# Revit family: QF_ELECTROLUXPROFESSIONAL_1L059Y_TD6-14_G
name_source: partatom
category: Attrezzature speciali
units: mm (PartAtom-declared; Revit-internal decimal feet)

## family parameters
Basato su piano di lavoro = No
Condiviso = No
Punto di calcolo locali = No
Quota connettore circolare = Usa diametro
Sempre verticale = Sì
Taglio con vuoti quando caricato = No
Tipo di parte = Normale

## types (36) — shared parameters
Depth Actual = 965 mm  [stored 3.16601 ft]
Height Actual = 1771 mm  [stored 5.81037 ft]
Latent Heat Output = 0.0
Length Actual = 790 mm  [stored 2.59186 ft]
Modello = TD6-14
Produttore = Electrolux Professional
Sensible Heat Output = 0.0
URL = www.electroluxprofessional.com
Weight = 222
zero-valued in all types: Prospetto di default, Steam Pounds per Hour

## per-type parameters (varying)
| type | Cycle | Descrizione | Gas KW | Item Number | Phase | Volts | Watts |
| 9873730032 | 50 Hz | TUMBLE DRYER TD6-14 14KG SST DRUM GAS 13,5KW 400/50/3 COMPASS PRO 6G82 EU SILVER DO.RIGHT STOP DISCON. | 13.5 | 1L0EDB | 3 | 400 V | 1000 W |
| 9873730150 | 50 Hz | TUMBLE DRYER TD6-14 14KG SST DRUM GAS 13,5KW 400/50/3N COMPASS PRO 6G81 EU SILVER DO.RIGHT MB STOP DISCON. | 13.5 | 1LSPA5 | 3 | 400 V | 1000 W |
| 9873730198 | 60 Hz | TUMBLE DRYER TD6-14 14KG GALVA.DRUM GAS 13,5KW 220/60/1N COMPASS PRO 6L80 EU SILVER DO.LEFT | 0 | 1L0H79 | 1 | 220 V | 1200 W |
| 9873730120 | 60 Hz | TUMBLE DRYER TD6-14 14KG GALVA.DRUM GAS 13,5KW 240/60/1N COMPASS PRO 6G82 EU SILVER DO.RIGHT STOP DISCON. | 13.5 | 1LSNV5 | 1 | 240 V | 1200 W |
| 9873730158 | 50 Hz | TUMBLE DRYER TD6-14 14KG GALVA.DRUM GAS 13,5KW 400/50/3N COMPASS PRO 6L80 EU SILVER DO.RIGHT.INS. EXT.PM. 2.I/O | 0 | 1L82DG | 3 | 400 V | 1000 W |
| 9873730108 | 50 Hz | TUMBLE DRYER TD6-14 14KG GALVA.DRUM GAS 13,5KW 400/50/3 COMPASS PRO 6G82 EU SILVER DO.RIGHT STOP DISCON. | 13.5 | 1LSNPR | 3 | 400 V | 1000 W |
| 9873730069 | 50 Hz | TUMBLE DRYER TD6-14 14KG SST DRUM GAS 13,5KW 400/50/3 COMPASS PRO 6L80 EU SILVER DO.RIGHT EXT.PM. DISCON. 2.I/O | 13.5 | 1LSN41 | 3 | 400 V | 1000 W |
| 9873730155 | 50 Hz | TUMBLE DRYER TD6-14 14KG SST DRUM GAS 13,5KW 400/50/3N COMPASS PRO 6L80 EU SILVER DO.RIGHT EXT.PM. DISCON. 2.I/O | 13.5 | 1LSPAA | 3 | 400 V | 1000 W |
| 9873730175 | 60 Hz | TUMBLE DRYER TD6-14 14KG GALVA.DRUM GAS 13,5KW 220/60/3 COMPASS PRO 6G81 EU SILVER DO.LEFT.INS. MB STOP DISCON. | 13.5 | 1L826B | 3 | 220 V | 1000 W |
| 9873730115 | 50 Hz | TUMBLE DRYER TD6-14 14KG GALVA.DRUM GAS 13,5KW 400/50/3 COMPASS PRO 6L80 EU SILVER DO.RIGHT | 13.5 | 1LSNSB | 3 | 400 V | 1000 W |
| 9873730152 | 50 Hz | TUMBLE DRYER TD6-14 14KG GALVA.DRUM GAS 13,5KW 400/50/3N COMPASS PRO 6G81 EU SILVER DO.RIGHT.INS. MB STOP DISCON. | 13.5 | 1LSPA7 | 3 | 400 V | 1000 W |
| 9873730014 | 50 Hz | TUMBLE DRYER TD6-14 14KG GALVA.DRUM GAS 13,5KW 400/50/3 COMPASS PRO 6G81 EU SILVER DO.RIGHT.INS. MB STOP DISCON. | 13.5 | 1L0E92 | 3 | 400 V | 1000 W |
| 9873730024 | 50 Hz | TUMBLE DRYER TD6-14 14KG GALVA.DRUM GAS 13,5KW 400/50/3 COMPASS PRO 6G81 EU SILVER DO.RIGHT MB STOP DISCON. | 13.5 | 1LSN2L | 3 | 400 V | 1000 W |
| 9873730083 | 50 Hz | TUMBLE DRYER TD6-14 14KG GALVA.DRUM GAS 13,5KW 400/50/3N COMPASS PRO 6G81 EU SILVER DO.RIGHT MB STOP DISCON. | 13.5 | 1LSN57 | 3 | 400 V | 1000 W |
| 9873730013 | 50 Hz | TUMBLE DRYER TD6-14 14KG GALVA.DRUM GAS 13,5KW 400/50/3 COMPASS PRO 6L80 EU SILVER DO.RIGHT.INS. EXT.PM. 2.I/O | 13.5 | 1L0E91 | 3 | 400 V | 1000 W |
| 9873730200 | 50 Hz | TUMBLE DRYER TD6-14 14KG SST DRUM GPL 13,5KW 200/50/3 COMPASS PRO 6G86 JP SILVER DO.RIGHT DISCON. | 0 | 1L0H7S | 3 | 200 V | 1000 W |
| 9873730033 | 50 Hz | TUMBLE DRYER TD6-14 14KG SST DRUM GAS 13,5KW 400/50/3 COMPASS PRO 6G81 EU SILVER DO.RIGHT MB STOP DISCON. | 13.5 | 1L0EDC | 3 | 400 V | 1000 W |
| 9873730197 | 60 Hz | TUMBLE DRYER TD6-14 14KG SST DRUM GPL 13,5KW 200/60/3 COMPASS PRO 6G86 JP SILVER DO.RIGHT DISCON. | 0 | 1LT5ZE | 3 | 200 V | 1000 W |
| 9873730107 | 50 Hz | TUMBLE DRYER TD6-14 14KG GALVA.DRUM GAS 13,5KW 230/50/1N COMPASS PRO 6G82 EU SILVER DO.RIGHT STOP DISCON. | 13.5 | 1LSNJN | 1 | 230 V | 1200 W |
| 9873730086 | 50 Hz | TUMBLE DRYER TD6-14 14KG GALVA.DRUM GAS 13,5KW 400/50/3 COMPASS PRO 6L80 EU SILVER DO.RIGHT EXT.PM. DISCON. 2.I/O | 13.5 | 1L8216 | 3 | 400 V | 1000 W |
| 9873730036 | 50 Hz | TUMBLE DRYER TD6-14 14KG GALVA.DRUM GAS 13,5KW 415/50/3N COMPASS PRO 6G82 EU SILVER DO.LEFT STOP DISCON. | 13.5 | 1L0EDR | 3 | 415 V | 1000 W |
| 9873730085 | 50 Hz | TUMBLE DRYER TD6-14 14KG GALVA.DRUM GAS 13,5KW 400/50/3N COMPASS PRO 6G81 EU SILVER DO.RIGHT.INS. ELS-NETW. MB STOP DISC | 13.5 | 1LSN61 | 3 | 400 V | 1000 W |
| 9873730151 | 50 Hz | TUMBLE DRYER TD6-14 14KG SST DRUM GAS 13,5KW 400/50/3N COMPASS PRO 6G82 EU SILVER DO.RIGHT STOP DISCON. | 13.5 | 1LSPA6 | 3 | 400 V | 1000 W |
| 9873730055 | 50 Hz | TUMBLE DRYER TD6-14 14KG GALVA.DRUM GAS 13,5KW 230/50/1N COMPASS PRO 6G81 EU SILVER DO.RIGHT MB STOP DISCON. | 13.5 | 1L80DU | 1 | 230 V | 1000 W |
| 9873730121 | 60 Hz | TUMBLE DRYER TD6-14 14KG GALVA.DRUM GAS 13,5KW 240/60/1N COMPASS PRO 6G81 EU SILVER DO.RIGHT MB STOP DISCON. | 13.5 | 1LSNV6 | 1 | 240 V | 1200 W |
| 9873730090 | 50 Hz | TUMBLE DRYER TD6-14 14KG GALVA.DRUM GAS 13,5KW 230/50/1N COMPASS PRO 6L80 EU SILVER DO.RIGHT EXT.PM. DISCON. 2.I/O | 13.5 | 1LSN8J | 1 | 230 V | 1200 W |
| 9873730035 | 50 Hz | TUMBLE DRYER TD6-14 14KG SST DRUM GAS 13,5KW 380-415/50/3N COMPASS PRO 6L80 EU SILVER DO.RIGHT DISCON. | 13.5 | 1L0EDD | 3 | 415 V | 1000 W |
| 9873730189 | 60 Hz | TUMBLE DRYER TD6-14 14KG GALVA.DRUM GAS 13,5KW 220/60/1N COMPASS PRO 6G82 EU SILVER DO.RIGHT STOP DISCON. EXT.CONN. | 0 | 1LSPPU | 1 | 220 V | 1200 W |
| 9873730149 | 50 Hz | TUMBLE DRYER TD6-14 14KG GALVA.DRUM GAS 13,5KW 400/50/3N COMPASS PRO 6G82 EU SILVER DO.RIGHT STOP DISCON. | 13.5 | 1LSPA4 | 3 | 400 V | 1000 W |
| 9873730060 | 50 Hz | TUMBLE DRYER TD6-14 14KG SST DRUM GAS 13,5KW 230/50/1N COMPASS PRO 6G82 EU SILVER DO.RIGHT STOP DISCON. | 13.5 | 1L80E4 | 1 | 230 V | 1200 W |
| 9873730211 | 50 Hz | TUMBLE DRYER TD6-14 14KG SST DRUM GAS 13,5KW 400/50/3N COMPASS PRO 6G81 EU SST/SILVER DO.RIGHT MB STOP DISCON. | 0 | 1L82DL | 3 | 400 V | 1000 W |
| 9873730196 | 60 Hz | TUMBLE DRYER TD6-14 14KG GALVA.DRUM GAS 13,5KW 220/60/3 COMPASS PRO 6G82 EU SILVER DO.LEFT STOP DISCON. EXT.CONN. | 0 | 1LSPR0 | 3 | 220 V | 1000 W |
| 9873730176 | 60 Hz | TUMBLE DRYER TD6-14 14KG GALVA.DRUM GAS 13,5KW 480/60/3 COMPASS PRO 6G81 EU SILVER DO.LEFT.INS. MB STOP DISCON. | 13.5 | 1L826K | 3 | 480 V | 1000 W |
| 9873730183 | 60 Hz | TUMBLE DRYER TD6-14 14KG SST DRUM GAS 13,5KW 380-415/60/3 COMPASS PRO 6G82 EU SST DO.RIGHT DSC STOP DISCON. | 13.5 | 1L0GZ1 | 3 | 415 V | 1000 W |
| 9873730087 | 60 Hz | TUMBLE DRYER TD6-14 14KG GALVA.DRUM GAS 13,5KW 208-240/60/1 COMPASS PRO 6G82 EU SILVER DO.LEFT STOP DISCON. | 13.5 | 1L0EKZ | 1 | 240 V | 1000 W |
| 9873730116 | 50 Hz | TUMBLE DRYER TD6-14 14KG SST DRUM GAS 13,5KW 230/50/1N COMPASS PRO 6L80 EU SILVER DO.RIGHT | 13.5 | 1LSNSC | 1 | 230 V | 1200 W |

note: [stored X ft] marks values corroborated as IEEE doubles in the binary element streams (Revit-internal decimal feet)

## geometry (parser evidence)
native form markers: Blend x14
no freeform markers — native parametric forms only
